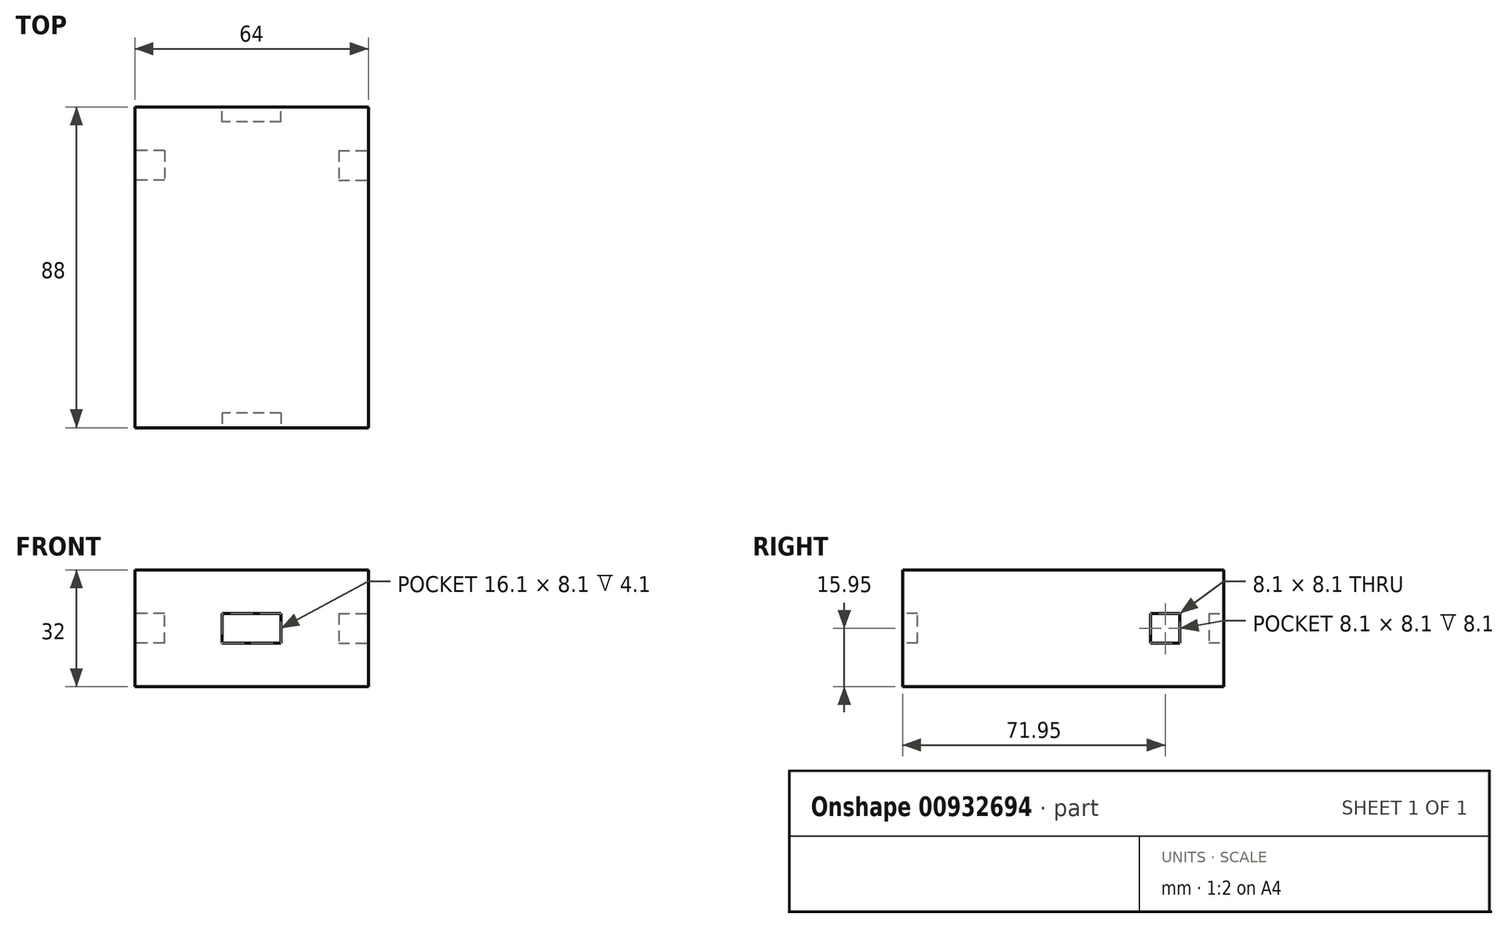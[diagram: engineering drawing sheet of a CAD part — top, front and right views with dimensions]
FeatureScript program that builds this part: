
annotation { "Feature Type Name" : "Feature", "Feature Type Description" : "" }
export const myFeature = defineFeature(function(context is Context, id is Id, definition is map)
    precondition{}
    {
        {
            var Q0;
            Q0=qCreatedBy(makeId("Top.planeOp"),FACE);
            var sketch = newSketch(context, id + "F0", { "sketchPlane" : qUnion([Q0])});
            skLineSegment(sketch, "E0.bottom", {"start": v(-32, 44) * mm, "end": v(32, 44) * mm});
            skLineSegment(sketch, "E0.left", {"start": v(-32, 44) * mm, "end": v(-32, -44) * mm});
            skLineSegment(sketch, "E0.right", {"start": v(32, 44) * mm, "end": v(32, -44) * mm});
            skLineSegment(sketch, "E1", {"start": v(-32, -44) * mm, "end": v(32, -44) * mm});
            skSolve(sketch);
        }
        {
            var Q0;
            Q0 = qSketchRegion(id + "F0", true);
            extrude(context, id + "F1", {"entities" : qUnion([Q0]), "depth" : 32 * mm, "offsetDistance" : 25 * mm});
        }
        {
            var Q0;
            Q0=makeQuery(id+"F1.opExtrude","SWEPT_FACE",FACE,{"disambiguationData":[OSD([sQuery(id+"F0.wireOp",EDGE,"E0.bottom")])]});
            var sketch = newSketch(context, id + "F2", { "sketchPlane" : qUnion([Q0])});
            skLineSegment(sketch, "E2.bottom", {"start": v(-8.05, 20.1) * mm, "end": v(8.05, 20.1) * mm});
            skLineSegment(sketch, "E2.top", {"start": v(-8.05, 12) * mm, "end": v(8.05, 12) * mm});
            skLineSegment(sketch, "E2.left", {"start": v(-8.05, 20.1) * mm, "end": v(-8.05, 12) * mm});
            skLineSegment(sketch, "E2.right", {"start": v(8.05, 20.1) * mm, "end": v(8.05, 12) * mm});
            skSolve(sketch);
        }
        {
            var Q0;
            Q0 = qSketchRegion(id + "F2", true);
            extrude(context, id + "F3", {"entities" : qUnion([Q0]), "operationType" : NewBodyOperationType.REMOVE, "oppositeDirection" : true, "depth" : 4.1 * mm, "offsetDistance" : 25 * mm});
        }
        {
            var Q0;
            Q0=makeQuery(id+"F1.opExtrude","SWEPT_FACE",FACE,{"disambiguationData":[OSD([sQuery(id+"F0.wireOp",EDGE,"E1")])]});
            var sketch = newSketch(context, id + "F4", { "sketchPlane" : qUnion([Q0])});
            skLineSegment(sketch, "E3.bottom", {"start": v(8.05, 11.9) * mm, "end": v(-8.05, 11.9) * mm});
            skLineSegment(sketch, "E3.top", {"start": v(8.05, 20) * mm, "end": v(-8.05, 20) * mm});
            skLineSegment(sketch, "E3.left", {"start": v(8.05, 11.9) * mm, "end": v(8.05, 20) * mm});
            skLineSegment(sketch, "E3.right", {"start": v(-8.05, 11.9) * mm, "end": v(-8.05, 20) * mm});
            skSolve(sketch);
        }
        {
            var Q0;
            Q0 = qSketchRegion(id + "F4", true);
            extrude(context, id + "F5", {"entities" : qUnion([Q0]), "operationType" : NewBodyOperationType.REMOVE, "oppositeDirection" : true, "depth" : 4.1 * mm, "offsetDistance" : 25 * mm});
        }
        {
            var Q0;
            Q0=makeQuery(id+"F1.opExtrude","SWEPT_FACE",FACE,{"disambiguationData":[OSD([sQuery(id+"F0.wireOp",EDGE,"E0.right")])]});
            var sketch = newSketch(context, id + "F6", { "sketchPlane" : qUnion([Q0])});
            skLineSegment(sketch, "E4.bottom", {"start": v(32, 20) * mm, "end": v(23.9, 20) * mm});
            skLineSegment(sketch, "E4.top", {"start": v(32, 11.9) * mm, "end": v(23.9, 11.9) * mm});
            skLineSegment(sketch, "E4.left", {"start": v(32, 20) * mm, "end": v(32, 11.9) * mm});
            skLineSegment(sketch, "E4.right", {"start": v(23.9, 20) * mm, "end": v(23.9, 11.9) * mm});
            skSolve(sketch);
        }
        {
            var Q0;
            Q0 = qSketchRegion(id + "F6", true);
            extrude(context, id + "F7", {"entities" : qUnion([Q0]), "operationType" : NewBodyOperationType.REMOVE, "oppositeDirection" : true, "depth" : 8.1 * mm, "offsetDistance" : 25 * mm});
        }
        {
            var Q0;
            Q0=makeQuery(id+"F1.opExtrude","SWEPT_FACE",FACE,{"disambiguationData":[OSD([sQuery(id+"F0.wireOp",EDGE,"E0.left")])]});
            var sketch = newSketch(context, id + "F8", { "sketchPlane" : qUnion([Q0])});
            skLineSegment(sketch, "E5.bottom", {"start": v(-32, 11.9) * mm, "end": v(-23.9, 11.9) * mm});
            skLineSegment(sketch, "E5.top", {"start": v(-32, 20) * mm, "end": v(-23.9, 20) * mm});
            skLineSegment(sketch, "E5.left", {"start": v(-32, 11.9) * mm, "end": v(-32, 20) * mm});
            skLineSegment(sketch, "E5.right", {"start": v(-23.9, 11.9) * mm, "end": v(-23.9, 20) * mm});
            skSolve(sketch);
        }
        {
            var Q0;
            Q0 = qSketchRegion(id + "F8", true);
            extrude(context, id + "F9", {"entities" : qUnion([Q0]), "operationType" : NewBodyOperationType.REMOVE, "oppositeDirection" : true, "depth" : 8.1 * mm, "offsetDistance" : 25 * mm});
        }
    });
